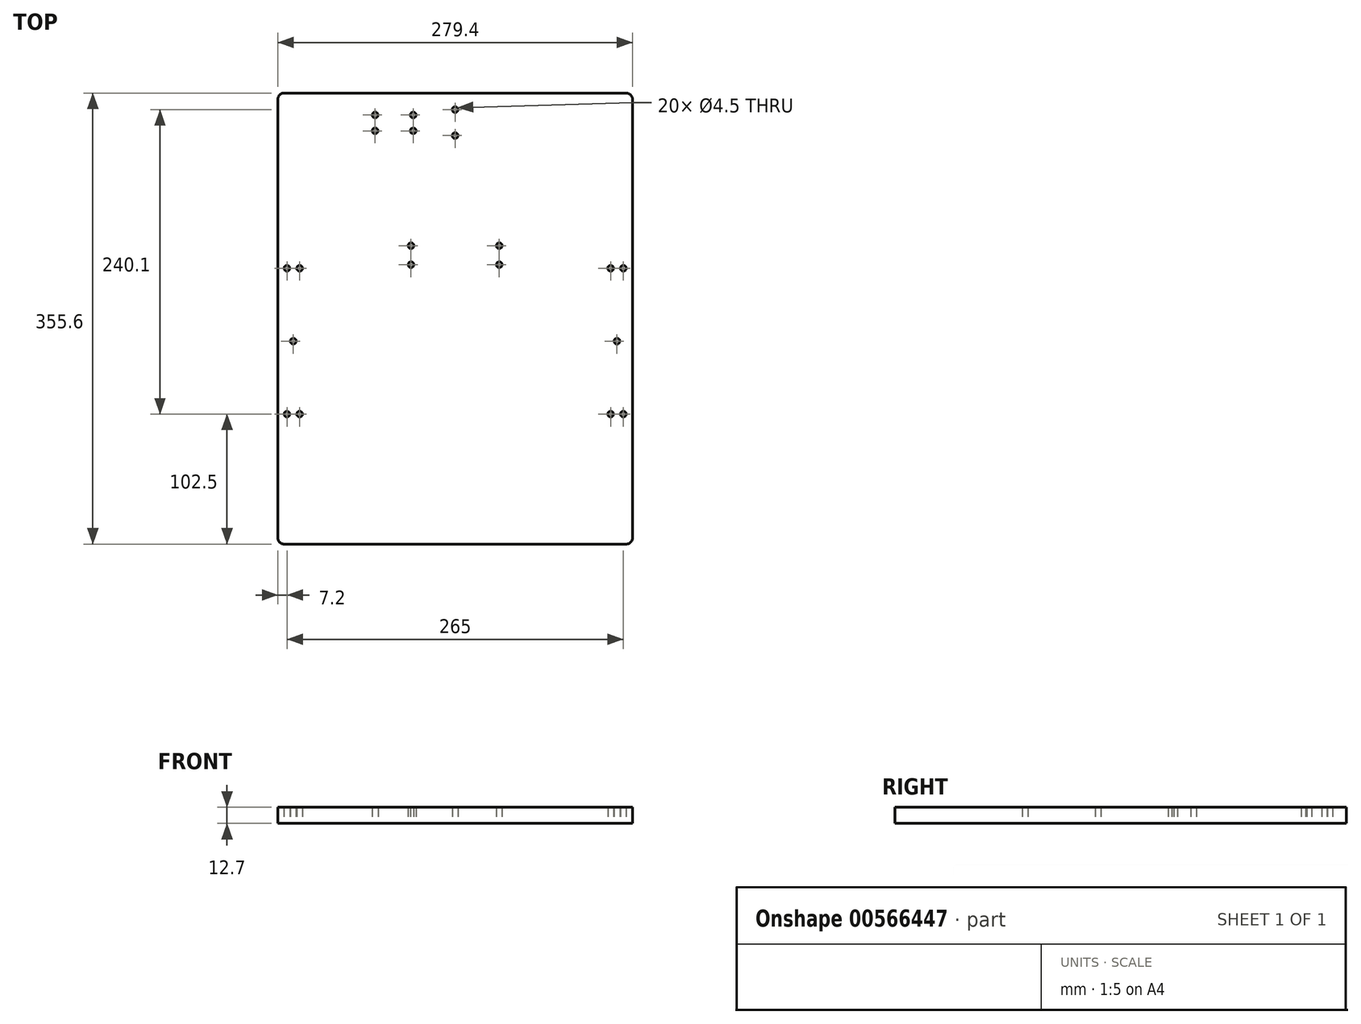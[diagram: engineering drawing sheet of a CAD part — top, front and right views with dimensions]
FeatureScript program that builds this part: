
annotation { "Feature Type Name" : "Feature", "Feature Type Description" : "" }
export const myFeature = defineFeature(function(context is Context, id is Id, definition is map)
    precondition{}
    {
        {
            var Q0;
            Q0=qCreatedBy(makeId("Top.planeOp"),FACE);
            var sketch = newSketch(context, id + "F0", { "sketchPlane" : qUnion([Q0])});
            skLineSegment(sketch, "E0.bottom", {"start": v(139.7, -177.8) * mm, "end": v(-139.7, -177.8) * mm});
            skLineSegment(sketch, "E0.top", {"start": v(139.7, 177.8) * mm, "end": v(-139.7, 177.8) * mm});
            skLineSegment(sketch, "E0.left", {"start": v(139.7, -177.8) * mm, "end": v(139.7, 177.8) * mm});
            skLineSegment(sketch, "E0.right", {"start": v(-139.7, -177.8) * mm, "end": v(-139.7, 177.8) * mm});
            skPoint(sketch, "E0.middle", {"position": v(0, 0) * mm});
            skLineSegment(sketch, "E1.bottom", {"start": v(-122.5, -75.3) * mm, "end": v(-132.5, -75.3) * mm, "construction": true});
            skLineSegment(sketch, "E1.top", {"start": v(-122.5, 39.7) * mm, "end": v(-132.5, 39.7) * mm, "construction": true});
            skLineSegment(sketch, "E1.left", {"start": v(-122.5, -75.3) * mm, "end": v(-122.5, 39.7) * mm, "construction": true});
            skLineSegment(sketch, "E1.right", {"start": v(-132.5, -75.3) * mm, "end": v(-132.5, 39.7) * mm, "construction": true});
            skPoint(sketch, "E1.middle", {"position": v(-127.5, -17.8) * mm});
            skCircle(sketch, "E2", {"center": v(-132.5, 39.7) * mm, "radius": 2.25 * mm});
            skCircle(sketch, "E3", {"center": v(-122.5, 39.7) * mm, "radius": 2.25 * mm});
            skCircle(sketch, "E4", {"center": v(-122.5, -75.3) * mm, "radius": 2.25 * mm});
            skCircle(sketch, "E5", {"center": v(-132.5, -75.3) * mm, "radius": 2.25 * mm});
            skCircle(sketch, "E6", {"center": v(-127.5, -17.8) * mm, "radius": 2.25 * mm});
            skCircle(sketch, "E7.MirrorC", {"center": v(122.5, -75.3) * mm, "radius": 2.25 * mm});
            skCircle(sketch, "E8.MirrorC", {"center": v(122.5, 39.7) * mm, "radius": 2.25 * mm});
            skCircle(sketch, "E9.MirrorC", {"center": v(132.5, 39.7) * mm, "radius": 2.25 * mm});
            skCircle(sketch, "E10.MirrorC", {"center": v(132.5, -75.3) * mm, "radius": 2.25 * mm});
            skCircle(sketch, "E11.MirrorC", {"center": v(127.5, -17.8) * mm, "radius": 2.25 * mm});
            skLineSegment(sketch, "E12.MirrorCS", {"start": v(132.5, -75.3) * mm, "end": v(132.5, 39.7) * mm, "construction": true});
            skLineSegment(sketch, "E13.MirrorCS", {"start": v(122.5, -75.3) * mm, "end": v(122.5, 39.7) * mm, "construction": true});
            skLineSegment(sketch, "E14.MirrorCS", {"start": v(122.5, 39.7) * mm, "end": v(132.5, 39.7) * mm, "construction": true});
            skLineSegment(sketch, "E15.MirrorCS", {"start": v(122.5, -75.3) * mm, "end": v(132.5, -75.3) * mm, "construction": true});
            skCircle(sketch, "E16", {"center": v(0, 164.8) * mm, "radius": 2.25 * mm});
            skCircle(sketch, "E17", {"center": v(0, 144.3) * mm, "radius": 2.25 * mm});
            skLineSegment(sketch, "E18.bottom", {"start": v(34.75, 42.5) * mm, "end": v(-34.75, 42.5) * mm, "construction": true});
            skLineSegment(sketch, "E18.top", {"start": v(34.75, 57.5) * mm, "end": v(-34.75, 57.5) * mm, "construction": true});
            skLineSegment(sketch, "E18.left", {"start": v(34.75, 42.5) * mm, "end": v(34.75, 57.5) * mm, "construction": true});
            skLineSegment(sketch, "E18.right", {"start": v(-34.75, 42.5) * mm, "end": v(-34.75, 57.5) * mm, "construction": true});
            skPoint(sketch, "E18.middle", {"position": v(0, 50) * mm});
            skCircle(sketch, "E19", {"center": v(-34.75, 57.5) * mm, "radius": 2.25 * mm});
            skCircle(sketch, "E20", {"center": v(-34.75, 42.5) * mm, "radius": 2.25 * mm});
            skCircle(sketch, "E21", {"center": v(34.75, 57.5) * mm, "radius": 2.25 * mm});
            skCircle(sketch, "E22", {"center": v(34.75, 42.5) * mm, "radius": 2.25 * mm});
            skCircle(sketch, "E23", {"center": v(33, 160.55) * mm, "radius": 2.25 * mm, "construction": true});
            skCircle(sketch, "E24", {"center": v(63, 160.55) * mm, "radius": 2.25 * mm, "construction": true});
            skLineSegment(sketch, "E25.bottom", {"start": v(63, 148.05) * mm, "end": v(33, 148.05) * mm, "construction": true});
            skLineSegment(sketch, "E25.top", {"start": v(63, 160.55) * mm, "end": v(33, 160.55) * mm, "construction": true});
            skLineSegment(sketch, "E25.left", {"start": v(63, 148.05) * mm, "end": v(63, 160.55) * mm, "construction": true});
            skLineSegment(sketch, "E25.right", {"start": v(33, 148.05) * mm, "end": v(33, 160.55) * mm, "construction": true});
            skPoint(sketch, "E25.middle", {"position": v(48, 154.3) * mm});
            skCircle(sketch, "E26", {"center": v(33, 148.05) * mm, "radius": 2.25 * mm, "construction": true});
            skCircle(sketch, "E27", {"center": v(63, 148.05) * mm, "radius": 2.25 * mm, "construction": true});
            skLineSegment(sketch, "E28.MirrorCS", {"start": v(-63, 148.05) * mm, "end": v(-33, 148.05) * mm, "construction": true});
            skCircle(sketch, "E29.MirrorC", {"center": v(-33, 148.05) * mm, "radius": 2.25 * mm});
            skCircle(sketch, "E30.MirrorC", {"center": v(-63, 160.55) * mm, "radius": 2.25 * mm});
            skLineSegment(sketch, "E31.MirrorCS", {"start": v(-33, 148.05) * mm, "end": v(-33, 160.55) * mm, "construction": true});
            skLineSegment(sketch, "E32.MirrorCS", {"start": v(-63, 160.55) * mm, "end": v(-33, 160.55) * mm, "construction": true});
            skLineSegment(sketch, "E33.MirrorCS", {"start": v(-63, 148.05) * mm, "end": v(-63, 160.55) * mm, "construction": true});
            skCircle(sketch, "E34.MirrorC", {"center": v(-63, 148.05) * mm, "radius": 2.25 * mm});
            skPoint(sketch, "E35.MirrorP", {"position": v(-48, 154.3) * mm});
            skCircle(sketch, "E36.MirrorC", {"center": v(-33, 160.55) * mm, "radius": 2.25 * mm});
            skSolve(sketch);
        }
        {
            var Q0;
            Q0=qSketchRegion(id+"F0",true);
            extrude(context, id + "F1", {"entities" : qUnion([Q0]), "depth" : 12.7 * mm, "offsetDistance" : 25 * mm});
        }
        {
            var Q0;
            Q0=makeQuery(id+"F1.opExtrude","SWEPT_EDGE",EDGE,{"disambiguationData":[OSD([sQuery(id+"F0.wireOp",EDGE,"E0.bottom"),sQuery(id+"F0.wireOp",EDGE,"E0.right")])]});
            var Q1;
            Q1=makeQuery(id+"F1.opExtrude","SWEPT_EDGE",EDGE,{"disambiguationData":[OSD([sQuery(id+"F0.wireOp",EDGE,"E0.bottom"),sQuery(id+"F0.wireOp",EDGE,"E0.left")])]});
            var Q2;
            Q2=makeQuery(id+"F1.opExtrude","SWEPT_EDGE",EDGE,{"disambiguationData":[OSD([sQuery(id+"F0.wireOp",EDGE,"E0.top"),sQuery(id+"F0.wireOp",EDGE,"E0.left")])]});
            var Q3;
            Q3=makeQuery(id+"F1.opExtrude","SWEPT_EDGE",EDGE,{"disambiguationData":[OSD([sQuery(id+"F0.wireOp",EDGE,"E0.top"),sQuery(id+"F0.wireOp",EDGE,"E0.right")])]});
            fillet(context, id + "F2", {"entities" : qUnion([Q0, Q1, Q2, Q3]), "radius" : 5 * mm, "tangentPropagation" : true, "allowEdgeOverflow" : false});
        }
    });
